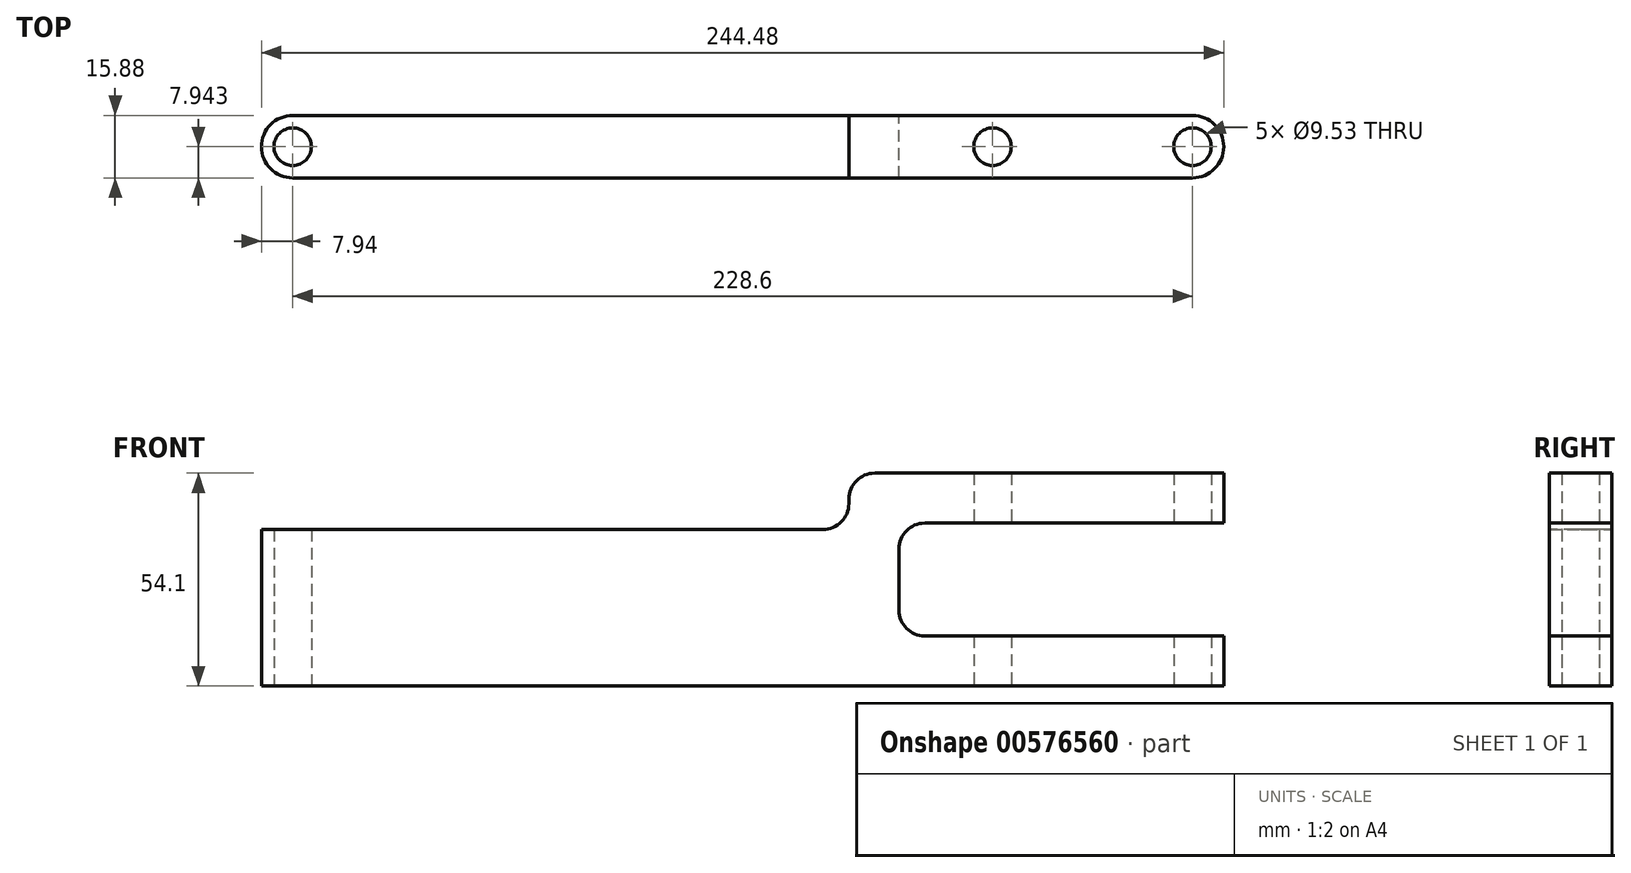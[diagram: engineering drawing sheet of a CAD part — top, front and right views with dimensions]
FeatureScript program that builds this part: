
annotation { "Feature Type Name" : "Feature", "Feature Type Description" : "" }
export const myFeature = defineFeature(function(context is Context, id is Id, definition is map)
    precondition{}
    {
        {
            var Q0;
            Q0=qCreatedBy(makeId("Top.planeOp"),FACE);
            var sketch = newSketch(context, id + "F0", { "sketchPlane" : qUnion([Q0])});
            skLineSegment(sketch, "E0.bottom", {"start": v(0, 0) * mm, "end": v(228.6, 0) * mm});
            skLineSegment(sketch, "E0.top", {"start": v(0, -15.88) * mm, "end": v(228.6, -15.88) * mm});
            skLineSegment(sketch, "E0.left", {"start": v(0, 0) * mm, "end": v(0, -15.88) * mm});
            skLineSegment(sketch, "E0.right", {"start": v(228.6, 0) * mm, "end": v(228.6, -15.88) * mm});
            skCircle(sketch, "E1", {"center": v(0, -7.94) * mm, "radius": 7.94 * mm});
            skCircle(sketch, "E2", {"center": v(228.6, -7.94) * mm, "radius": 7.94 * mm});
            skPoint(sketch, "E3", {"position": v(177.8, -7.94) * mm});
            skSolve(sketch);
        }
        {
            var Q0;
            {var subQ0=sQuery(id+"F0.wireOp",EDGE,"E0.right");Q0=makeQuery(id+"F0.imprint","IMPRINT",FACE,{"disambiguationData":[TD([[makeQuery(id+"F0.imprint","IMPRINT",EDGE,{"derivedFrom":subQ0}),1.0]])]});}
            var Q1;
            {var subQ0=sQuery(id+"F0.wireOp",EDGE,"E0.right");Q1=makeQuery(id+"F0.imprint","IMPRINT",FACE,{"disambiguationData":[TD([[makeQuery(id+"F0.imprint","IMPRINT",EDGE,{"derivedFrom":subQ0}),-1.0]])]});}
            var Q2;
            {var subQ0=sQuery(id+"F0.wireOp",EDGE,"E0.bottom");Q2=makeQuery(id+"F0.imprint","IMPRINT",FACE,{"disambiguationData":[TD([[makeQuery(id+"F0.imprint","IMPRINT",EDGE,{"derivedFrom":subQ0}),-1.0]])]});}
            var Q3;
            {var subQ0=sQuery(id+"F0.wireOp",EDGE,"E0.left");Q3=makeQuery(id+"F0.imprint","IMPRINT",FACE,{"disambiguationData":[TD([[makeQuery(id+"F0.imprint","IMPRINT",EDGE,{"derivedFrom":subQ0}),1.0]])]});}
            var Q4;
            {var subQ0=sQuery(id+"F0.wireOp",EDGE,"E0.left");Q4=makeQuery(id+"F0.imprint","IMPRINT",FACE,{"disambiguationData":[TD([[makeQuery(id+"F0.imprint","IMPRINT",EDGE,{"derivedFrom":subQ0}),-1.0]])]});}
            extrude(context, id + "F1", {"entities" : qUnion([Q0, Q1, Q2, Q3, Q4]), "depth" : 54.1 * mm, "offsetDistance" : 25.4 * mm});
        }
        {
            var Q0;
            Q0=sQuery(id+"F0.wireOp",VERTEX,"E1.center");
            var Q1;
            Q1=sQuery(id+"F0.wireOp",VERTEX,"E3");
            var Q2;
            Q2=sQuery(id+"F0.wireOp",VERTEX,"E2.center");
            var Q3;
            Q3=makeQuery(id+"F1.opExtrude","SWEPT_BODY",BODY,{"disambiguationData":[OSD([sQuery(id+"F0.wireOp",EDGE,"E0.bottom"),sQuery(id+"F0.wireOp",EDGE,"E0.top"),sQuery(id+"F0.wireOp",EDGE,"E1"),sQuery(id+"F0.wireOp",EDGE,"E2")])]});
            hole(context, id + "F2", {"style" : HoleStyle.SIMPLE, "endStyle" : HoleEndStyle.THROUGH, "oppositeDirection" : true, "holeDiameter" : 9.52 * mm, "isTappedThrough" : true, "tappedDepth" : 12.7 * mm, "tapClearance" : 3, "locations" : qUnion([Q0, Q1, Q2]), "scope" : qUnion([Q3])});
        }
        {
            var Q0;
            Q0=qCreatedBy(makeId("Front.planeOp"),FACE);
            var sketch = newSketch(context, id + "F3", { "sketchPlane" : qUnion([Q0])});
            skLineSegment(sketch, "E4.0.0", {"start": v(228.6, 0) * mm, "end": v(0, 0) * mm});
            skLineSegment(sketch, "E4.0.1", {"start": v(0, 0) * mm, "end": v(0, 54.1) * mm});
            skLineSegment(sketch, "E4.0.2", {"start": v(0, 54.1) * mm, "end": v(228.6, 54.1) * mm});
            skLineSegment(sketch, "E4.0.3", {"start": v(228.6, 54.1) * mm, "end": v(228.6, 0) * mm});
            skLineSegment(sketch, "E5.0.0", {"start": v(228.6, 0) * mm, "end": v(236.54, 0) * mm});
            skLineSegment(sketch, "E5.0.1", {"start": v(228.6, 0) * mm, "end": v(228.6, 54.1) * mm});
            skLineSegment(sketch, "E5.0.2", {"start": v(228.6, 54.1) * mm, "end": v(236.54, 54.1) * mm});
            skLineSegment(sketch, "E6.0.1", {"start": v(228.6, 54.1) * mm, "end": v(0, 54.1) * mm});
            skLineSegment(sketch, "E6.0.2", {"start": v(0, 54.1) * mm, "end": v(-7.94, 54.1) * mm});
            skLineSegment(sketch, "E7.0.0", {"start": v(0, 0) * mm, "end": v(7.94, 0) * mm});
            skLineSegment(sketch, "E7.0.1", {"start": v(0, 0) * mm, "end": v(228.6, 0) * mm});
            skLineSegment(sketch, "E7.0.2", {"start": v(228.6, 0) * mm, "end": v(220.66, 0) * mm});
            skLineSegment(sketch, "E8.0", {"start": v(-7.94, 0) * mm, "end": v(7.94, 0) * mm});
            skLineSegment(sketch, "E9", {"start": v(-7.94, 27.05) * mm, "end": v(236.54, 27.05) * mm, "construction": true});
            skLineSegment(sketch, "E10", {"start": v(-7.94, 0) * mm, "end": v(-7.94, 54.1) * mm, "construction": true});
            skLineSegment(sketch, "E11", {"start": v(236.54, 0) * mm, "end": v(236.54, 54.1) * mm, "construction": true});
            skLineSegment(sketch, "E12.bottom", {"start": v(153.99, 12.7) * mm, "end": v(264.83, 12.7) * mm});
            skLineSegment(sketch, "E12.top", {"start": v(153.99, 41.4) * mm, "end": v(264.83, 41.4) * mm});
            skLineSegment(sketch, "E12.left", {"start": v(153.99, 12.7) * mm, "end": v(153.99, 41.4) * mm});
            skLineSegment(sketch, "E12.right", {"start": v(264.83, 12.7) * mm, "end": v(264.83, 41.4) * mm});
            skLineSegment(sketch, "E13.0", {"start": v(182.56, 0) * mm, "end": v(173.04, 0) * mm});
            skLineSegment(sketch, "E14.0", {"start": v(182.56, 54.1) * mm, "end": v(173.04, 54.1) * mm});
            skSolve(sketch);
        }
        {
            var Q0;
            Q0=qCreatedBy(makeId("Front.planeOp"),FACE);
            var sketch = newSketch(context, id + "F4", { "sketchPlane" : qUnion([Q0])});
            skLineSegment(sketch, "E15.bottom", {"start": v(-20.64, 39.75) * mm, "end": v(141.29, 39.75) * mm});
            skLineSegment(sketch, "E15.top", {"start": v(-20.64, 66.8) * mm, "end": v(141.29, 66.8) * mm});
            skLineSegment(sketch, "E15.left", {"start": v(-20.64, 39.75) * mm, "end": v(-20.64, 66.8) * mm});
            skLineSegment(sketch, "E15.right", {"start": v(141.29, 39.75) * mm, "end": v(141.29, 66.8) * mm});
            skLineSegment(sketch, "E16.0", {"start": v(-7.94, 27.05) * mm, "end": v(236.54, 27.05) * mm});
            skLineSegment(sketch, "E17.0", {"start": v(153.99, 12.7) * mm, "end": v(153.99, 41.4) * mm});
            skSolve(sketch);
        }
        {
            var Q0;
            {var subQ5=sQuery(id+"F3.wireOp",EDGE,"E12.left");Q0=makeQuery(id+"F3.imprint","IMPRINT",FACE,{"disambiguationData":[TD([[makeQuery(id+"F3.imprint","IMPRINT",EDGE,{"derivedFrom":subQ5}),-1.0]])]});}
            var Q1;
            {var subQ5=sQuery(id+"F3.wireOp",EDGE,"E12.right");Q1=makeQuery(id+"F3.imprint","IMPRINT",FACE,{"disambiguationData":[TD([[makeQuery(id+"F3.imprint","IMPRINT",EDGE,{"derivedFrom":subQ5}),1.0]])]});}
            var Q2;
            Q2=makeQuery(id+"F4.imprint","IMPRINT",FACE,{"disambiguationData":[TD([[makeQuery(id+"F4.imprint","IMPRINT",EDGE,{"derivedFrom":sQuery(id+"F4.wireOp",EDGE,"E15.bottom")}),1.0]])]});
            extrude(context, id + "F5", {"entities" : qUnion([Q0, Q1, Q2]), "operationType" : NewBodyOperationType.REMOVE, "depth" : 25.4 * mm, "offsetDistance" : 25.4 * mm});
        }
        {
            var Q0;
            Q0=makeQuery(id+"F1.opExtrude","CAP_FACE",FACE,{"disambiguationData":[OSD([sQuery(id+"F0.wireOp",EDGE,"E0.bottom"),sQuery(id+"F0.wireOp",EDGE,"E0.top"),sQuery(id+"F0.wireOp",EDGE,"E1"),sQuery(id+"F0.wireOp",EDGE,"E2")])],"isStart":false});
            var Q1;
            {var subQ0=sQuery(id+"F0.wireOp",EDGE,"E0.bottom");Q1=makeQuery(id+"F0.imprint","IMPRINT",FACE,{"disambiguationData":[TD([[makeQuery(id+"F0.imprint","IMPRINT",EDGE,{"derivedFrom":subQ0}),-1.0]])]});}
            cPlane(context, id + "F6", {"entities" : qUnion([Q0, Q1]), "cplaneType" : CPlaneType.MID_PLANE, "offset" : 25.4 * mm, "width" : 152.4 * mm, "height" : 152.4 * mm});
        }
        {
            var Q0;
            Q0=makeQuery(id+"F5.boolean.opBoolean","COPY",EDGE,{"derivedFrom":makeQuery(id+"F5.opExtrude","SWEPT_EDGE",EDGE,{"disambiguationData":[OSD([sQuery(id+"F4.wireOp",EDGE,"E15.bottom"),sQuery(id+"F4.wireOp",EDGE,"E15.right")])]})});
            var Q1;
            Q1=makeQuery(id+"F5.boolean.opBoolean","INTERSECT",EDGE,{"derivedFrom":[makeQuery(id+"F1.opExtrude","CAP_FACE",FACE,{"disambiguationData":[OSD([sQuery(id+"F0.wireOp",EDGE,"E0.bottom"),sQuery(id+"F0.wireOp",EDGE,"E0.top"),sQuery(id+"F0.wireOp",EDGE,"E1"),sQuery(id+"F0.wireOp",EDGE,"E2")])],"isStart":false}),makeQuery(id+"F5.opExtrude","SWEPT_FACE",FACE,{"disambiguationData":[OSD([sQuery(id+"F4.wireOp",EDGE,"E15.right")])]})]});
            var Q2;
            Q2=makeQuery(id+"F1v86Yb0eyvBsqd_1.1.F5.boolean.opBoolean","COPY",EDGE,{"derivedFrom":makeQuery(id+"F1v86Yb0eyvBsqd_1.1.F5.opExtrude","SWEPT_EDGE",EDGE,{"disambiguationData":[OSD([sQuery(id+"F4.wireOp",EDGE,"E15.bottom"),sQuery(id+"F4.wireOp",EDGE,"E15.right")])]})});
            var Q3;
            Q3=makeQuery(id+"F1v86Yb0eyvBsqd_1.1.F5.boolean.opBoolean","INTERSECT",EDGE,{"derivedFrom":[makeQuery(id+"F1.opExtrude","CAP_FACE",FACE,{"disambiguationData":[OSD([sQuery(id+"F0.wireOp",EDGE,"E0.bottom"),sQuery(id+"F0.wireOp",EDGE,"E0.top"),sQuery(id+"F0.wireOp",EDGE,"E1"),sQuery(id+"F0.wireOp",EDGE,"E2")])],"isStart":true}),makeQuery(id+"F1v86Yb0eyvBsqd_1.1.F5.opExtrude","SWEPT_FACE",FACE,{"disambiguationData":[OSD([sQuery(id+"F4.wireOp",EDGE,"E15.right")])]})]});
            var Q4;
            Q4=makeQuery(id+"F5.boolean.opBoolean","COPY",EDGE,{"derivedFrom":makeQuery(id+"F5.opExtrude","SWEPT_EDGE",EDGE,{"disambiguationData":[OSD([sQuery(id+"F3.wireOp",EDGE,"E12.bottom"),sQuery(id+"F3.wireOp",EDGE,"E12.left")])]})});
            var Q5;
            Q5=makeQuery(id+"F5.boolean.opBoolean","COPY",EDGE,{"derivedFrom":makeQuery(id+"F5.opExtrude","SWEPT_EDGE",EDGE,{"disambiguationData":[OSD([sQuery(id+"F3.wireOp",EDGE,"E12.top"),sQuery(id+"F3.wireOp",EDGE,"E12.left")])]})});
            fillet(context, id + "F7", {"entities" : qUnion([Q0, Q1, Q2, Q3, Q4, Q5]), "radius" : 6.6 * mm, "tangentPropagation" : true, "allowEdgeOverflow" : false});
        }
    });
